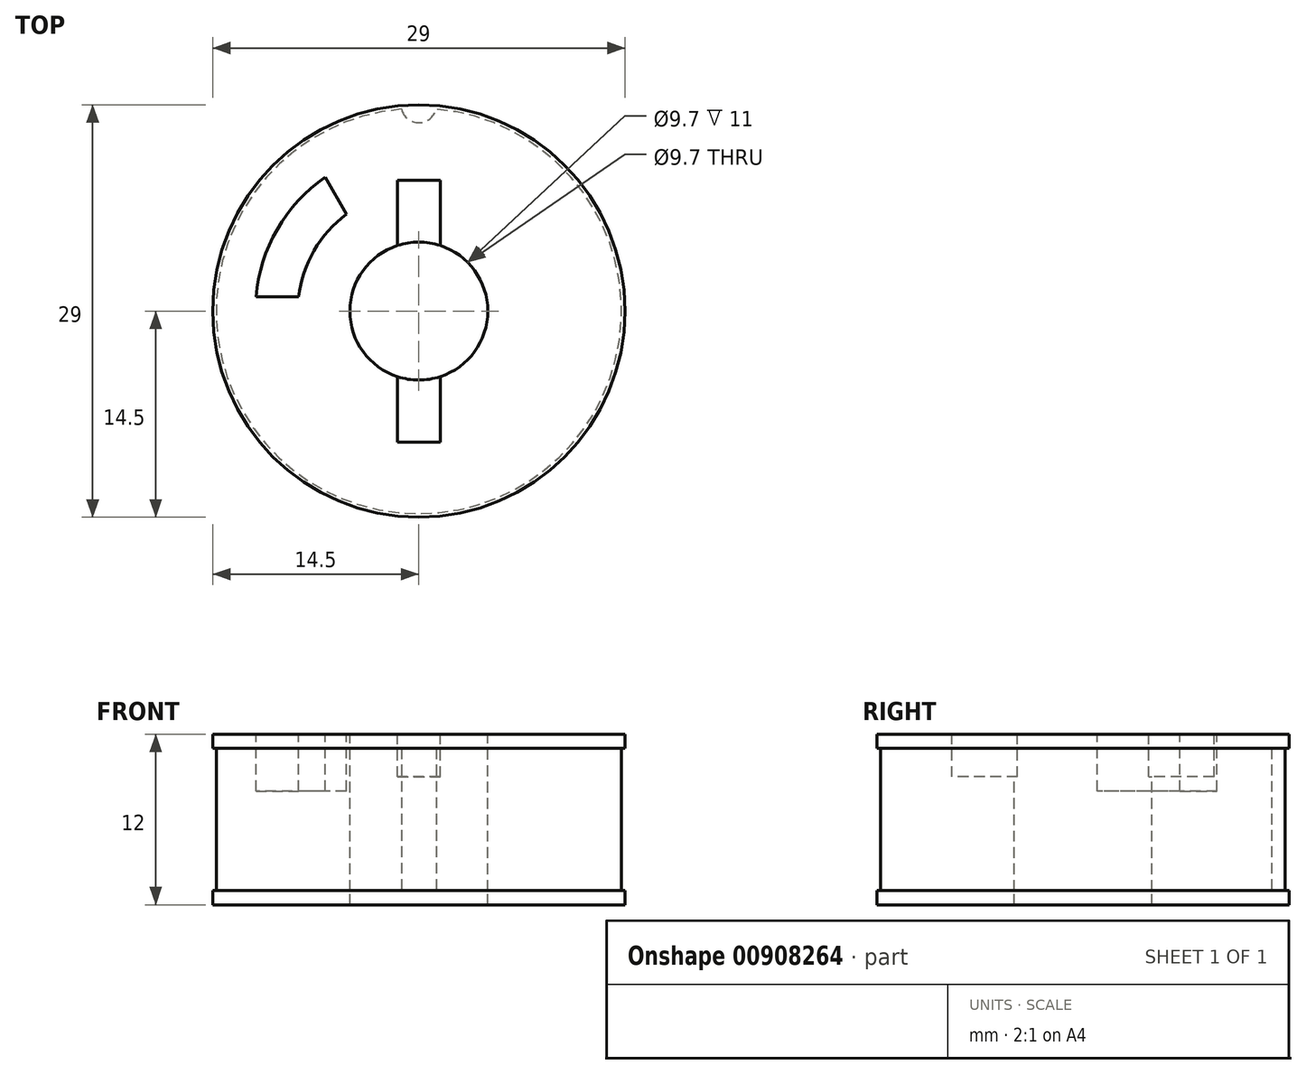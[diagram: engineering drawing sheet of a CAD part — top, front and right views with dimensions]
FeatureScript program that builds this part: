
annotation { "Feature Type Name" : "Feature", "Feature Type Description" : "" }
export const myFeature = defineFeature(function(context is Context, id is Id, definition is map)
    precondition{}
    {
        {
            var Q0;
            Q0=qCreatedBy(makeId("Top.planeOp"),FACE);
            var sketch = newSketch(context, id + "F0", { "sketchPlane" : qUnion([Q0])});
            skCircle(sketch, "E0", {"center": v(0, 0) * mm, "radius": 14.5 * mm});
            skSolve(sketch);
        }
        {
            var Q0;
            Q0 = qSketchRegion(id + "F0", true);
            extrude(context, id + "F1", {"entities" : qUnion([Q0]), "depth" : 1 * mm, "offsetDistance" : 25 * mm});
        }
        {
            var Q0;
            Q0=makeQuery(id+"F1.opExtrude","CAP_FACE",FACE,{"disambiguationData":[OSD([sQuery(id+"F0.wireOp",EDGE,"E0")])],"isStart":false});
            var sketch = newSketch(context, id + "F2", { "sketchPlane" : qUnion([Q0])});
            skCircle(sketch, "E1", {"center": v(0, 0) * mm, "radius": 14.5 * mm});
            skSolve(sketch);
        }
        {
            var Q0;
            Q0 = qSketchRegion(id + "F2", true);
            extrude(context, id + "F3", {"entities" : qUnion([Q0]), "depth" : 11 * mm, "offsetDistance" : 25 * mm});
        }
        {
            var Q0;
            Q0=makeQuery(id+"F3.opExtrude","CAP_FACE",FACE,{"disambiguationData":[OSD([sQuery(id+"F2.wireOp",EDGE,"E1")])],"isStart":true});
            var sketch = newSketch(context, id + "F4", { "sketchPlane" : qUnion([Q0])});
            skCircle(sketch, "E2", {"center": v(0, -14.5) * mm, "radius": 1.25 * mm});
            skSolve(sketch);
        }
        {
            var Q0;
            Q0 = qSketchRegion(id + "F4", true);
            extrude(context, id + "F5", {"entities" : qUnion([Q0]), "operationType" : NewBodyOperationType.REMOVE, "oppositeDirection" : true, "depth" : 10 * mm, "offsetDistance" : 25 * mm});
        }
        {
            var Q0;
            Q0=makeQuery(id+"F3.opExtrude","CAP_FACE",FACE,{"disambiguationData":[OSD([sQuery(id+"F2.wireOp",EDGE,"E1")])],"isStart":true});
            var sketch = newSketch(context, id + "F6", { "sketchPlane" : qUnion([Q0])});
            skCircle(sketch, "E3", {"center": v(0, 0) * mm, "radius": 14.5 * mm});
            skCircle(sketch, "E4", {"center": v(0, 0) * mm, "radius": 14.25 * mm});
            skSolve(sketch);
        }
        {
            var Q0;
            Q0 = qSketchRegion(id + "F6", true);
            extrude(context, id + "F7", {"entities" : qUnion([Q0]), "operationType" : NewBodyOperationType.REMOVE, "oppositeDirection" : true, "depth" : 10 * mm, "offsetDistance" : 25 * mm});
        }
        {
            var Q0;
            Q0=makeQuery(id+"F3.opExtrude","CAP_FACE",FACE,{"disambiguationData":[OSD([sQuery(id+"F2.wireOp",EDGE,"E1")])],"isStart":false});
            var sketch = newSketch(context, id + "F8", { "sketchPlane" : qUnion([Q0])});
            skLineSegment(sketch, "E5", {"start": v(-10.35, 0) * mm, "end": v(-1.95, 0) * mm, "construction": true});
            skArc(sketch, "E6", {"start": v(-6.6, 9.42) * mm, "mid": v(-9.96, 5.75) * mm, "end": v(-11.46, 1) * mm});
            skArc(sketch, "E7", {"start": v(-5.09, 6.81) * mm, "mid": v(-7.36, 4.25) * mm, "end": v(-8.44, 1) * mm});
            skLineSegment(sketch, "E8", {"start": v(-11.46, 1) * mm, "end": v(-8.44, 1) * mm});
            skLineSegment(sketch, "E9", {"start": v(0, 0) * mm, "end": v(-9.22, 15.97) * mm, "construction": true});
            skLineSegment(sketch, "E10", {"start": v(-5.09, 6.81) * mm, "end": v(-6.6, 9.42) * mm});
            skSolve(sketch);
        }
        {
            var Q0;
            Q0 = qSketchRegion(id + "F8", true);
            extrude(context, id + "F9", {"entities" : qUnion([Q0]), "operationType" : NewBodyOperationType.REMOVE, "oppositeDirection" : true, "depth" : 4 * mm, "offsetDistance" : 25 * mm});
        }
        {
            var Q0;
            Q0=makeQuery(id+"F3.opExtrude","CAP_FACE",FACE,{"disambiguationData":[OSD([sQuery(id+"F2.wireOp",EDGE,"E1")])],"isStart":false});
            var sketch = newSketch(context, id + "F10", { "sketchPlane" : qUnion([Q0])});
            skCircle(sketch, "E11", {"center": v(0, 0) * mm, "radius": 4.85 * mm});
            skSolve(sketch);
        }
        {
            var Q0;
            Q0 = qSketchRegion(id + "F10", true);
            extrude(context, id + "F11", {"entities" : qUnion([Q0]), "operationType" : NewBodyOperationType.REMOVE, "endBound" : BoundingType.THROUGH_ALL, "oppositeDirection" : true, "depth" : 25 * mm, "offsetDistance" : 25 * mm});
        }
        {
            var Q0;
            Q0=makeQuery(id+"F3.opExtrude","CAP_FACE",FACE,{"disambiguationData":[OSD([sQuery(id+"F2.wireOp",EDGE,"E1")])],"isStart":false});
            var sketch = newSketch(context, id + "F12", { "sketchPlane" : qUnion([Q0])});
            skLineSegment(sketch, "E12.bottom", {"start": v(-1.5, 9.21) * mm, "end": v(1.5, 9.21) * mm});
            skLineSegment(sketch, "E12.top", {"start": v(-1.5, -9.21) * mm, "end": v(1.5, -9.21) * mm});
            skLineSegment(sketch, "E12.left", {"start": v(-1.5, 9.21) * mm, "end": v(-1.5, -9.21) * mm});
            skLineSegment(sketch, "E12.right", {"start": v(1.5, 9.21) * mm, "end": v(1.5, -9.21) * mm});
            skPoint(sketch, "E12.middle", {"position": v(0, 0) * mm});
            skSolve(sketch);
        }
        {
            var Q0;
            Q0 = qSketchRegion(id + "F12", true);
            extrude(context, id + "F13", {"entities" : qUnion([Q0]), "operationType" : NewBodyOperationType.REMOVE, "oppositeDirection" : true, "depth" : 3 * mm, "offsetDistance" : 25 * mm});
        }
    });
